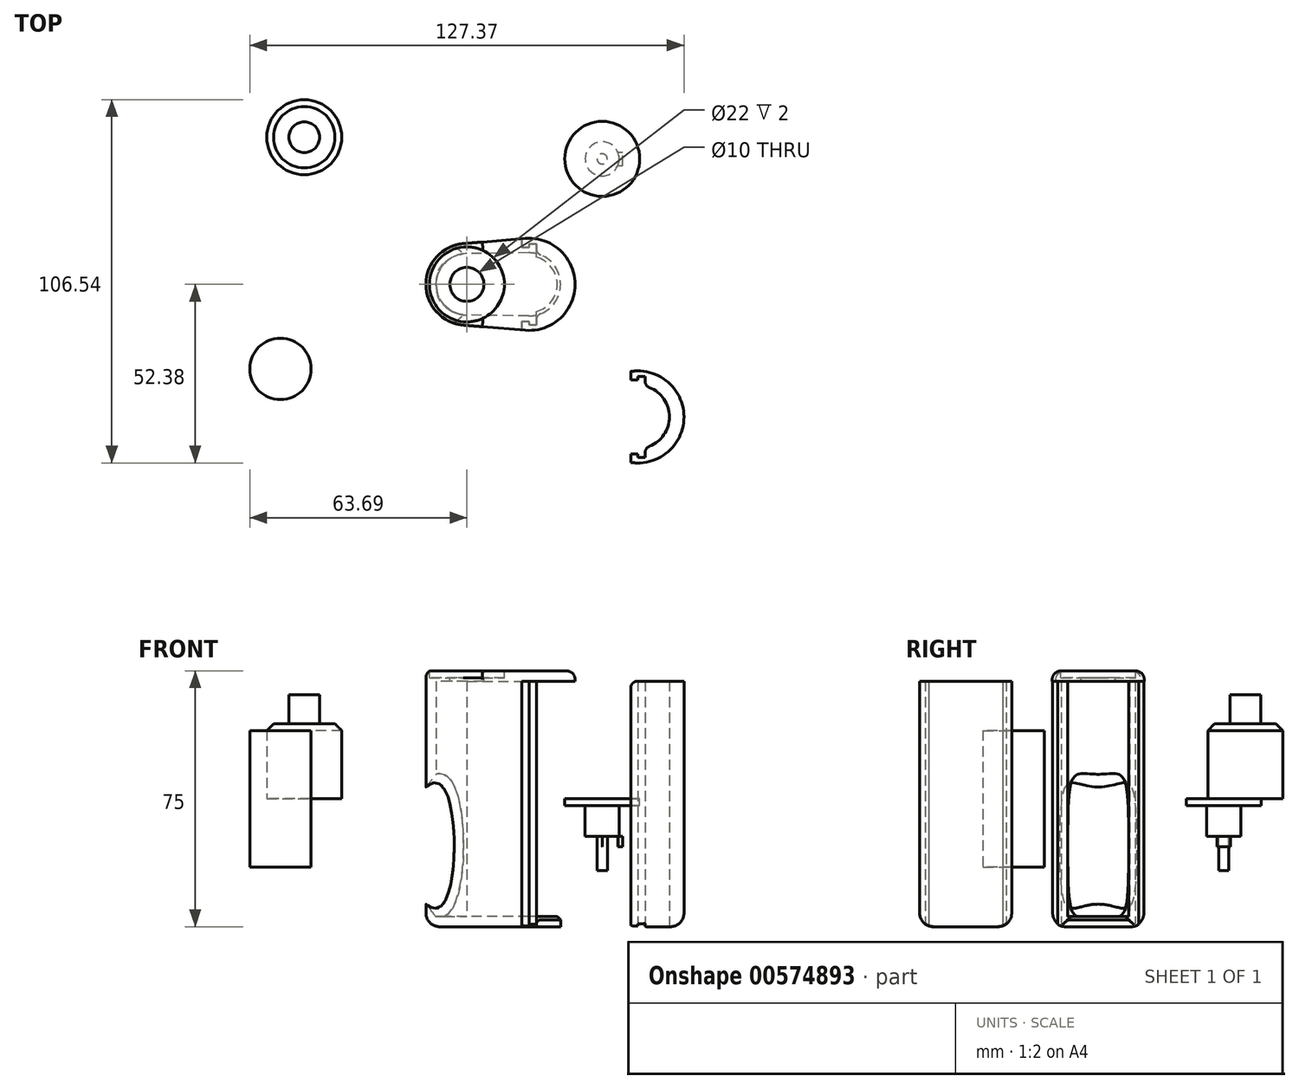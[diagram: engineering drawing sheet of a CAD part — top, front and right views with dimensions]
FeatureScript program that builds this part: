
annotation { "Feature Type Name" : "Feature", "Feature Type Description" : "" }
export const myFeature = defineFeature(function(context is Context, id is Id, definition is map)
    precondition{}
    {
        {
            var Q0;
            Q0=qCreatedBy(makeId("Top.planeOp"),FACE);
            var sketch = newSketch(context, id + "F0", { "sketchPlane" : qUnion([Q0])});
            skArc(sketch, "E0", {"start": v(20.38, 9) * mm, "mid": v(19.26, 9.2) * mm, "end": v(18.12, 9.25) * mm});
            skArc(sketch, "E1", {"start": v(-0.99, 11.96) * mm, "mid": v(-12, 0) * mm, "end": v(-0.99, -11.96) * mm});
            skArc(sketch, "E2", {"start": v(17.14, -13.45) * mm, "mid": v(31.75, 0) * mm, "end": v(17.14, 13.45) * mm});
            skLineSegment(sketch, "E3", {"start": v(17.14, 13.45) * mm, "end": v(-0.99, 11.96) * mm});
            skLineSegment(sketch, "E4", {"start": v(-0.99, -11.96) * mm, "end": v(17.14, -13.45) * mm});
            skPoint(sketch, "E5", {"position": v(18.25, 11.38) * mm});
            skPoint(sketch, "E6", {"position": v(18.25, -11.38) * mm});
            skLineSegment(sketch, "E7", {"start": v(18.25, 11.38) * mm, "end": v(18.25, 11.9) * mm});
            skLineSegment(sketch, "E8", {"start": v(18.25, 11.38) * mm, "end": v(18.25, 10.85) * mm});
            skLineSegment(sketch, "E9", {"start": v(18.25, -11.38) * mm, "end": v(18.25, -10.85) * mm});
            skLineSegment(sketch, "E10", {"start": v(18.25, -11.38) * mm, "end": v(18.25, -11.9) * mm});
            skLineSegment(sketch, "E11", {"start": v(18.25, -11.9) * mm, "end": v(20.38, -11.9) * mm});
            skLineSegment(sketch, "E12", {"start": v(18.25, -10.85) * mm, "end": v(16.12, -10.85) * mm});
            skLineSegment(sketch, "E13", {"start": v(18.25, 10.85) * mm, "end": v(16.13, 10.85) * mm});
            skLineSegment(sketch, "E14", {"start": v(18.25, 11.9) * mm, "end": v(20.38, 11.9) * mm});
            skLineSegment(sketch, "E15", {"start": v(16.13, 10.85) * mm, "end": v(16.13, 13.37) * mm});
            skLineSegment(sketch, "E16", {"start": v(20.38, 11.9) * mm, "end": v(20.38, 9) * mm});
            skLineSegment(sketch, "E17", {"start": v(16.12, -10.85) * mm, "end": v(16.12, -13.37) * mm});
            skLineSegment(sketch, "E18", {"start": v(20.38, -11.9) * mm, "end": v(20.38, -9) * mm});
            skPoint(sketch, "E19.orphan", {"position": v(16.13, 11.38) * mm});
            skPoint(sketch, "E20.end.orphan", {"position": v(20.38, 11.38) * mm});
            skPoint(sketch, "E21.orphan", {"position": v(16.12, -11.38) * mm});
            skPoint(sketch, "E22.end.orphan", {"position": v(20.38, -11.38) * mm});
            skArc(sketch, "E23", {"start": v(0, 9) * mm, "mid": v(-9, 0) * mm, "end": v(0, -9) * mm});
            skLineSegment(sketch, "E24", {"start": v(0, 9) * mm, "end": v(18.12, 9.25) * mm});
            skLineSegment(sketch, "E25", {"start": v(0, -9) * mm, "end": v(18.12, -9.25) * mm});
            skArc(sketch, "E26.trimOffspring", {"start": v(18.12, -9.25) * mm, "mid": v(19.26, -9.2) * mm, "end": v(20.37, -9) * mm});
            skSolve(sketch);
        }
        {
            var Q0;
            Q0=makeQuery(id+"F0.imprint","IMPRINT",FACE,{"disambiguationData":[TD([[makeQuery(id+"F0.imprint","IMPRINT",EDGE,{"derivedFrom":sQuery(id+"F0.wireOp",EDGE,"E0")}),-1.0]])]});
            extrude(context, id + "F1", {"entities" : qUnion([Q0]), "endBound" : BoundingType.SYMMETRIC, "depth" : 75 * mm, "offsetDistance" : 25 * mm});
        }
        {
            var Q0;
            Q0=makeQuery(id+"F1.opExtrude","CAP_FACE",FACE,{"disambiguationData":[OSD([sQuery(id+"F0.wireOp",EDGE,"E0"),sQuery(id+"F0.wireOp",EDGE,"E1"),sQuery(id+"F0.wireOp",EDGE,"E3"),sQuery(id+"F0.wireOp",EDGE,"E4"),sQuery(id+"F0.wireOp",EDGE,"E7"),sQuery(id+"F0.wireOp",EDGE,"E8"),sQuery(id+"F0.wireOp",EDGE,"E9"),sQuery(id+"F0.wireOp",EDGE,"E10"),sQuery(id+"F0.wireOp",EDGE,"E11"),sQuery(id+"F0.wireOp",EDGE,"E12"),sQuery(id+"F0.wireOp",EDGE,"E13"),sQuery(id+"F0.wireOp",EDGE,"E14"),sQuery(id+"F0.wireOp",EDGE,"E15"),sQuery(id+"F0.wireOp",EDGE,"E16"),sQuery(id+"F0.wireOp",EDGE,"E17"),sQuery(id+"F0.wireOp",EDGE,"E18"),sQuery(id+"F0.wireOp",EDGE,"E23"),sQuery(id+"F0.wireOp",EDGE,"E24"),sQuery(id+"F0.wireOp",EDGE,"E25"),sQuery(id+"F0.wireOp",EDGE,"E26.trimOffspring")])],"isStart":false});
            var sketch = newSketch(context, id + "F2", { "sketchPlane" : qUnion([Q0])});
            skArc(sketch, "E27", {"start": v(-0.99, 11.96) * mm, "mid": v(-12, 0) * mm, "end": v(-0.99, -11.96) * mm});
            skArc(sketch, "E28", {"start": v(17.14, -13.45) * mm, "mid": v(31.75, 0) * mm, "end": v(17.14, 13.45) * mm});
            skLineSegment(sketch, "E29", {"start": v(17.14, 13.45) * mm, "end": v(-0.99, 11.96) * mm});
            skLineSegment(sketch, "E30", {"start": v(-0.99, -11.96) * mm, "end": v(17.14, -13.45) * mm});
            skPoint(sketch, "E31", {"position": v(18.25, 11.38) * mm});
            skPoint(sketch, "E32", {"position": v(18.25, -11.38) * mm});
            skPoint(sketch, "E33.orphan", {"position": v(16.12, 11.38) * mm});
            skPoint(sketch, "E34.end.orphan", {"position": v(20.38, 11.38) * mm});
            skPoint(sketch, "E35.orphan", {"position": v(16.12, -11.38) * mm});
            skPoint(sketch, "E36.end.orphan", {"position": v(20.38, -11.38) * mm});
            skPoint(sketch, "E37.start.orphan", {"position": v(16.12, 10.85) * mm});
            skPoint(sketch, "E38.orphan", {"position": v(20.38, 11.9) * mm});
            skPoint(sketch, "E39.start.orphan", {"position": v(18.25, -11.9) * mm});
            skPoint(sketch, "E40.start.orphan", {"position": v(20.38, -11.9) * mm});
            skPoint(sketch, "E41.orphan", {"position": v(16.12, -10.85) * mm});
            skSolve(sketch);
        }
        {
            var Q0;
            {var subQ0=sQuery(id+"F2.wireOp",EDGE,"E28");Q0=makeQuery(id+"F2.imprint","IMPRINT",FACE,{"disambiguationData":[TD([[makeQuery(id+"F2.imprint","IMPRINT",EDGE,{"derivedFrom":subQ0}),1.0]])]});}
            var Q1;
            Q1 = qSketchRegion(id + "F4", true);
            extrude(context, id + "F3", {"entities" : qUnion([Q0, Q1]), "operationType" : NewBodyOperationType.ADD, "oppositeDirection" : true, "depth" : 3 * mm, "offsetDistance" : 25 * mm});
        }
        {
            var Q0;
            Q0=makeQuery(id+"F1.opExtrude","CAP_FACE",FACE,{"disambiguationData":[OSD([sQuery(id+"F0.wireOp",EDGE,"E0"),sQuery(id+"F0.wireOp",EDGE,"E1"),sQuery(id+"F0.wireOp",EDGE,"E3"),sQuery(id+"F0.wireOp",EDGE,"E4"),sQuery(id+"F0.wireOp",EDGE,"E7"),sQuery(id+"F0.wireOp",EDGE,"E8"),sQuery(id+"F0.wireOp",EDGE,"E9"),sQuery(id+"F0.wireOp",EDGE,"E10"),sQuery(id+"F0.wireOp",EDGE,"E11"),sQuery(id+"F0.wireOp",EDGE,"E12"),sQuery(id+"F0.wireOp",EDGE,"E13"),sQuery(id+"F0.wireOp",EDGE,"E14"),sQuery(id+"F0.wireOp",EDGE,"E15"),sQuery(id+"F0.wireOp",EDGE,"E16"),sQuery(id+"F0.wireOp",EDGE,"E17"),sQuery(id+"F0.wireOp",EDGE,"E18"),sQuery(id+"F0.wireOp",EDGE,"E23"),sQuery(id+"F0.wireOp",EDGE,"E24"),sQuery(id+"F0.wireOp",EDGE,"E25"),sQuery(id+"F0.wireOp",EDGE,"E26.trimOffspring")])],"isStart":true});
            var sketch = newSketch(context, id + "F4", { "sketchPlane" : qUnion([Q0])});
            skArc(sketch, "E42", {"start": v(-0.99, 11.96) * mm, "mid": v(-12, 0) * mm, "end": v(-0.99, -11.96) * mm});
            skLineSegment(sketch, "E43", {"start": v(16.12, 13.37) * mm, "end": v(-0.99, 11.96) * mm});
            skLineSegment(sketch, "E44", {"start": v(-0.99, -11.96) * mm, "end": v(16.13, -13.37) * mm});
            skPoint(sketch, "E45", {"position": v(18.25, 11.38) * mm});
            skPoint(sketch, "E46", {"position": v(18.25, -11.38) * mm});
            skLineSegment(sketch, "E47", {"start": v(18.25, 11.38) * mm, "end": v(18.25, 11.9) * mm});
            skLineSegment(sketch, "E48", {"start": v(18.25, 11.38) * mm, "end": v(18.25, 10.85) * mm});
            skLineSegment(sketch, "E49", {"start": v(18.25, -11.38) * mm, "end": v(18.25, -10.85) * mm});
            skLineSegment(sketch, "E50", {"start": v(18.25, -11.38) * mm, "end": v(18.25, -11.9) * mm});
            skLineSegment(sketch, "E51", {"start": v(18.25, -11.9) * mm, "end": v(20.38, -11.9) * mm});
            skLineSegment(sketch, "E52", {"start": v(18.25, -10.85) * mm, "end": v(16.12, -10.85) * mm});
            skLineSegment(sketch, "E53", {"start": v(18.25, 10.85) * mm, "end": v(16.12, 10.85) * mm});
            skLineSegment(sketch, "E54", {"start": v(18.25, 11.9) * mm, "end": v(20.38, 11.9) * mm});
            skLineSegment(sketch, "E55", {"start": v(16.12, 10.85) * mm, "end": v(16.12, 13.37) * mm});
            skLineSegment(sketch, "E56", {"start": v(20.38, 11.9) * mm, "end": v(20.38, 9) * mm});
            skLineSegment(sketch, "E57", {"start": v(16.12, -10.85) * mm, "end": v(16.12, -13.37) * mm});
            skLineSegment(sketch, "E58", {"start": v(20.38, -11.9) * mm, "end": v(20.38, -9) * mm});
            skPoint(sketch, "E59.orphan", {"position": v(16.12, 11.38) * mm});
            skPoint(sketch, "E60.end.orphan", {"position": v(20.38, 11.38) * mm});
            skPoint(sketch, "E61.orphan", {"position": v(16.12, -11.38) * mm});
            skPoint(sketch, "E62.end.orphan", {"position": v(20.38, -11.38) * mm});
            skArc(sketch, "E63", {"start": v(20.38, -9) * mm, "mid": v(27.5, 0) * mm, "end": v(20.38, 9) * mm});
            skSolve(sketch);
        }
        {
            var Q0;
            Q0 = qSketchRegion(id + "F4", true);
            extrude(context, id + "F5", {"entities" : qUnion([Q0]), "operationType" : NewBodyOperationType.ADD, "oppositeDirection" : true, "depth" : 3 * mm, "offsetDistance" : 25 * mm});
        }
        {
            var Q0;
            {var subQ0=sQuery(id+"F0.wireOp",EDGE,"E26.trimOffspring");var subQ1=sQuery(id+"F0.wireOp",EDGE,"E25");var subQ2=sQuery(id+"F0.wireOp",EDGE,"E24");var subQ3=sQuery(id+"F0.wireOp",EDGE,"E23");var subQ4=sQuery(id+"F0.wireOp",EDGE,"E18");var subQ5=sQuery(id+"F0.wireOp",EDGE,"E17");var subQ6=sQuery(id+"F0.wireOp",EDGE,"E16");var subQ7=sQuery(id+"F0.wireOp",EDGE,"E15");var subQ8=sQuery(id+"F0.wireOp",EDGE,"E14");var subQ9=sQuery(id+"F0.wireOp",EDGE,"E13");var subQ10=sQuery(id+"F0.wireOp",EDGE,"E12");var subQ11=sQuery(id+"F0.wireOp",EDGE,"E11");var subQ12=sQuery(id+"F0.wireOp",EDGE,"E10");var subQ13=sQuery(id+"F0.wireOp",EDGE,"E9");var subQ14=sQuery(id+"F0.wireOp",EDGE,"E8");var subQ15=sQuery(id+"F0.wireOp",EDGE,"E7");var subQ16=sQuery(id+"F0.wireOp",EDGE,"E0");Q0=makeQuery(id+"F3.boolean.opBoolean","MERGE",FACE,{"derivedFrom":[makeQuery(id+"F1.opExtrude","CAP_FACE",FACE,{"disambiguationData":[OSD([subQ16,sQuery(id+"F0.wireOp",EDGE,"E1"),sQuery(id+"F0.wireOp",EDGE,"E3"),sQuery(id+"F0.wireOp",EDGE,"E4"),subQ15,subQ14,subQ13,subQ12,subQ11,subQ10,subQ9,subQ8,subQ7,subQ6,subQ5,subQ4,subQ3,subQ2,subQ1,subQ0])],"isStart":false}),makeQuery(id+"F3.opExtrude","CAP_FACE",FACE,{"disambiguationData":[OSD([subQ16,subQ15,subQ14,subQ13,subQ12,subQ11,subQ10,subQ9,subQ8,subQ7,subQ6,subQ5,subQ4,subQ3,subQ2,subQ1,subQ0,sQuery(id+"F2.wireOp",EDGE,"E28"),sQuery(id+"F2.wireOp",EDGE,"E29"),sQuery(id+"F2.wireOp",EDGE,"E30")])],"isStart":true})]});}
            var sketch = newSketch(context, id + "F6", { "sketchPlane" : qUnion([Q0])});
            skCircle(sketch, "E64", {"center": v(0, 0) * mm, "radius": 11 * mm});
            skSolve(sketch);
        }
        {
            var Q0;
            Q0=makeQuery(id+"F6.imprint","IMPRINT",FACE,{"disambiguationData":[TD([[makeQuery(id+"F6.imprint","IMPRINT",EDGE,{"derivedFrom":sQuery(id+"F6.wireOp",EDGE,"E64")}),1.0]])]});
            extrude(context, id + "F7", {"entities" : qUnion([Q0]), "operationType" : NewBodyOperationType.REMOVE, "oppositeDirection" : true, "depth" : 2 * mm, "offsetDistance" : 25 * mm});
        }
        {
            var Q0;
            Q0=makeQuery(id+"F7.boolean.opBoolean","COPY",FACE,{"derivedFrom":makeQuery(id+"F7.opExtrude","CAP_FACE",FACE,{"disambiguationData":[OSD([sQuery(id+"F6.wireOp",EDGE,"E64")])],"isStart":false})});
            var sketch = newSketch(context, id + "F8", { "sketchPlane" : qUnion([Q0])});
            skCircle(sketch, "E65", {"center": v(0, 0) * mm, "radius": 5 * mm});
            skSolve(sketch);
        }
        {
            var Q0;
            Q0=makeQuery(id+"F8.imprint","IMPRINT",FACE,{"disambiguationData":[TD([[makeQuery(id+"F8.imprint","IMPRINT",EDGE,{"derivedFrom":sQuery(id+"F8.wireOp",EDGE,"E65")}),1.0]])]});
            var Q1;
            Q1=sQuery(id+"F8.wireOp",EDGE,"E65");
            extrude(context, id + "F9", {"entities" : qUnion([Q0]), "operationType" : NewBodyOperationType.REMOVE, "surfaceEntities" : qUnion([Q1]), "oppositeDirection" : true, "depth" : 13.8 * mm, "offsetDistance" : 25 * mm});
        }
        {
            var Q0;
            Q0=qCreatedBy(makeId("Top.planeOp"),FACE);
            var sketch = newSketch(context, id + "F10", { "sketchPlane" : qUnion([Q0])});
            skArc(sketch, "E66", {"start": v(52.3, -47.88) * mm, "mid": v(59.43, -38.88) * mm, "end": v(52.3, -29.88) * mm});
            skArc(sketch, "E67", {"start": v(49.08, -52.33) * mm, "mid": v(63.68, -38.88) * mm, "end": v(49.08, -25.43) * mm});
            skLineSegment(sketch, "E68", {"start": v(49.08, -25.43) * mm, "end": v(48.06, -25.5) * mm});
            skLineSegment(sketch, "E69", {"start": v(48.06, -52.25) * mm, "end": v(49.08, -52.33) * mm});
            skPoint(sketch, "E70", {"position": v(50.18, -27.5) * mm});
            skPoint(sketch, "E71", {"position": v(50.18, -50.26) * mm});
            skLineSegment(sketch, "E72", {"start": v(50.18, -27.5) * mm, "end": v(50.18, -26.98) * mm});
            skLineSegment(sketch, "E73", {"start": v(50.18, -27.5) * mm, "end": v(50.18, -28.04) * mm});
            skLineSegment(sketch, "E74", {"start": v(50.18, -50.26) * mm, "end": v(50.18, -49.73) * mm});
            skLineSegment(sketch, "E75", {"start": v(50.18, -50.26) * mm, "end": v(50.18, -50.79) * mm});
            skLineSegment(sketch, "E76", {"start": v(50.18, -50.79) * mm, "end": v(52.3, -50.79) * mm});
            skLineSegment(sketch, "E77", {"start": v(50.18, -49.73) * mm, "end": v(48.06, -49.73) * mm});
            skLineSegment(sketch, "E78", {"start": v(50.18, -28.04) * mm, "end": v(48.06, -28.04) * mm});
            skLineSegment(sketch, "E79", {"start": v(50.18, -26.98) * mm, "end": v(52.3, -26.98) * mm});
            skLineSegment(sketch, "E80", {"start": v(48.06, -28.04) * mm, "end": v(48.06, -25.5) * mm});
            skLineSegment(sketch, "E81", {"start": v(52.3, -26.98) * mm, "end": v(52.3, -29.88) * mm});
            skLineSegment(sketch, "E82", {"start": v(48.06, -49.73) * mm, "end": v(48.06, -52.25) * mm});
            skLineSegment(sketch, "E83", {"start": v(52.3, -50.79) * mm, "end": v(52.3, -47.88) * mm});
            skPoint(sketch, "E84.orphan", {"position": v(52.3, -27.5) * mm});
            skPoint(sketch, "E85.start.orphan", {"position": v(48.06, -27.5) * mm});
            skPoint(sketch, "E86.orphan", {"position": v(52.3, -50.26) * mm});
            skPoint(sketch, "E87.start.orphan", {"position": v(48.06, -50.26) * mm});
            skSolve(sketch);
        }
        {
            var Q0;
            Q0=makeQuery(id+"F10.imprint","IMPRINT",FACE,{"disambiguationData":[TD([[makeQuery(id+"F10.imprint","IMPRINT",EDGE,{"derivedFrom":sQuery(id+"F10.wireOp",EDGE,"E66")}),-1.0]])]});
            extrude(context, id + "F11", {"entities" : qUnion([Q0]), "depth" : 34.5 * mm, "offsetDistance" : 25 * mm, "hasSecondDirection" : true, "secondDirectionOppositeDirection" : true, "secondDirectionDepth" : 37.5 * mm});
        }
        {
            var Q0;
            Q0=qCreatedBy(makeId("Top.planeOp"),FACE);
            var sketch = newSketch(context, id + "F12", { "sketchPlane" : qUnion([Q0])});
            skCircle(sketch, "E88", {"center": v(-47.7, 43.16) * mm, "radius": 11 * mm});
            skSolve(sketch);
        }
        {
            var Q0;
            Q0=makeQuery(id+"F12.imprint","IMPRINT",FACE,{"disambiguationData":[TD([[makeQuery(id+"F12.imprint","IMPRINT",EDGE,{"derivedFrom":sQuery(id+"F12.wireOp",EDGE,"E88")}),1.0]])]});
            extrude(context, id + "F13", {"entities" : qUnion([Q0]), "depth" : 22 * mm, "offsetDistance" : 25 * mm});
        }
        {
            var Q0;
            Q0=makeQuery(id+"F13.opExtrude","CAP_FACE",FACE,{"disambiguationData":[OSD([sQuery(id+"F12.wireOp",EDGE,"E88")])],"isStart":false});
            var sketch = newSketch(context, id + "F14", { "sketchPlane" : qUnion([Q0])});
            skCircle(sketch, "E89", {"center": v(-47.7, 43.16) * mm, "radius": 4.5 * mm});
            skSolve(sketch);
        }
        {
            var Q0;
            Q0=makeQuery(id+"F14.imprint","IMPRINT",FACE,{"disambiguationData":[TD([[makeQuery(id+"F14.imprint","IMPRINT",EDGE,{"derivedFrom":sQuery(id+"F14.wireOp",EDGE,"E89")}),1.0]])]});
            extrude(context, id + "F15", {"entities" : qUnion([Q0]), "operationType" : NewBodyOperationType.ADD, "depth" : 8.5 * mm, "offsetDistance" : 25 * mm});
        }
        {
            var Q0;
            Q0=makeQuery(id+"F13.opExtrude","CAP_EDGE",EDGE,{"disambiguationData":[OSD([sQuery(id+"F12.wireOp",EDGE,"E88")])],"isStart":false});
            chamfer(context, id + "F16", {"entities" : qUnion([Q0]), "width" : 2 * mm, "tangentPropagation" : true});
        }
        {
            var Q0;
            Q0=qCreatedBy(makeId("Front.planeOp"),FACE);
            var sketch = newSketch(context, id + "F17", { "sketchPlane" : qUnion([Q0])});
            skEllipse(sketch, "E90", {"center": v(-13.2, -13.71) * mm, "majorRadius": 15.12 * mm, "minorRadius": 5.56 * mm, "majorAxis": v(0, -1)});
            skSolve(sketch);
        }
        {
            var Q0;
            Q0 = qSketchRegion(id + "F17", true);
            var Q1;
            Q1=makeQuery(id+"F17.imprint","IMPRINT",FACE,{"disambiguationData":[TD([[makeQuery(id+"F17.imprint","IMPRINT",EDGE,{"derivedFrom":sQuery(id+"F17.wireOp",EDGE,"E90")}),1.0]])]});
            extrude(context, id + "F18", {"entities" : qUnion([Q0, Q1]), "operationType" : NewBodyOperationType.REMOVE, "endBound" : BoundingType.SYMMETRIC, "oppositeDirection" : true, "depth" : 25 * mm, "offsetDistance" : 25 * mm});
        }
        {
            var Q0;
            Q0=makeQuery(id+"F18.boolean.opBoolean","INTERSECT",EDGE,{"derivedFrom":[makeQuery(id+"F1.opExtrude","SWEPT_FACE",FACE,{"disambiguationData":[OSD([sQuery(id+"F0.wireOp",EDGE,"E23")])]}),makeQuery(id+"F18.opExtrude","SWEPT_FACE",FACE,{"disambiguationData":[OSD([sQuery(id+"F17.wireOp",EDGE,"E90")])]})]});
            chamfer(context, id + "F19", {"entities" : qUnion([Q0]), "width" : 6 * mm, "tangentPropagation" : true});
        }
        {
            var Q0;
            Q0=qCreatedBy(makeId("Top.planeOp"),FACE);
            var sketch = newSketch(context, id + "F20", { "sketchPlane" : qUnion([Q0])});
            skCircle(sketch, "E91", {"center": v(-54.69, -24.8) * mm, "radius": 9 * mm});
            skSolve(sketch);
        }
        {
            var Q0;
            Q0=makeQuery(id+"F20.imprint","IMPRINT",FACE,{"disambiguationData":[TD([[makeQuery(id+"F20.imprint","IMPRINT",EDGE,{"derivedFrom":sQuery(id+"F20.wireOp",EDGE,"E91")}),1.0]])]});
            extrude(context, id + "F21", {"entities" : qUnion([Q0]), "endBound" : BoundingType.SYMMETRIC, "depth" : 40 * mm, "offsetDistance" : 25 * mm});
        }
        {
            var Q0;
            Q0=makeQuery(id+"F1.opExtrude","CAP_EDGE",EDGE,{"disambiguationData":[OSD([sQuery(id+"F0.wireOp",EDGE,"E1")])],"isStart":true});
            var Q1;
            Q1=makeQuery(id+"F11.opExtrude","CAP_EDGE",EDGE,{"disambiguationData":[OSD([sQuery(id+"F10.wireOp",EDGE,"E67")])],"isStart":true});
            var Q2;
            Q2=makeQuery(id+"F18.boolean.opBoolean","INTERSECT",EDGE,{"derivedFrom":[makeQuery(id+"F1.opExtrude","SWEPT_FACE",FACE,{"disambiguationData":[OSD([sQuery(id+"F0.wireOp",EDGE,"E1")])]}),makeQuery(id+"F18.opExtrude","SWEPT_FACE",FACE,{"disambiguationData":[OSD([sQuery(id+"F17.wireOp",EDGE,"E90")])]})]});
            fillet(context, id + "F22", {"entities" : qUnion([Q0, Q1, Q2]), "radius" : 4 * mm, "tangentPropagation" : true, "allowEdgeOverflow" : false});
        }
        {
            var Q0;
            Q0=makeQuery(id+"F3.opExtrude","CAP_EDGE",EDGE,{"disambiguationData":[OSD([sQuery(id+"F2.wireOp",EDGE,"E28")])],"isStart":true});
            fillet(context, id + "F23", {"entities" : qUnion([Q0]), "radius" : 2.5 * mm, "tangentPropagation" : true, "allowEdgeOverflow" : false});
        }
        {
            var Q0;
            Q0=makeQuery(id+"F3.opExtrude","CAP_EDGE",EDGE,{"disambiguationData":[OSD([sQuery(id+"F0.wireOp",EDGE,"E17")])],"isStart":false});
            var Q1;
            Q1=makeQuery(id+"F3.opExtrude","CAP_EDGE",EDGE,{"disambiguationData":[OSD([sQuery(id+"F0.wireOp",EDGE,"E15")])],"isStart":false});
            var Q2;
            Q2=makeQuery(id+"F11.opExtrude","CAP_EDGE",EDGE,{"disambiguationData":[OSD([sQuery(id+"F10.wireOp",EDGE,"E80")])],"isStart":false});
            var Q3;
            Q3=makeQuery(id+"F11.opExtrude","CAP_EDGE",EDGE,{"disambiguationData":[OSD([sQuery(id+"F10.wireOp",EDGE,"E82")])],"isStart":false});
            fillet(context, id + "F24", {"entities" : qUnion([Q0, Q1, Q2, Q3]), "radius" : 2 * mm, "tangentPropagation" : true, "allowEdgeOverflow" : false});
        }
        {
            var Q0;
            Q0=makeQuery(id+"F5.opExtrude","CAP_EDGE",EDGE,{"disambiguationData":[OSD([sQuery(id+"F4.wireOp",EDGE,"E63")])],"isStart":false});
            chamfer(context, id + "F25", {"entities" : qUnion([Q0]), "width" : 1 * mm, "tangentPropagation" : true});
        }
        {
            var Q0;
            Q0=makeQuery(id+"F11.opExtrude","SWEPT_EDGE",EDGE,{"disambiguationData":[OSD([sQuery(id+"F10.wireOp",EDGE,"E66"),sQuery(id+"F10.wireOp",EDGE,"E81")])]});
            var Q1;
            Q1=makeQuery(id+"F11.opExtrude","SWEPT_EDGE",EDGE,{"disambiguationData":[OSD([sQuery(id+"F10.wireOp",EDGE,"E66"),sQuery(id+"F10.wireOp",EDGE,"E83")])]});
            fillet(context, id + "F26", {"entities" : qUnion([Q0, Q1]), "radius" : 2 * mm, "tangentPropagation" : true, "allowEdgeOverflow" : false});
        }
        {
            var Q0;
            {var subQ0=sQuery(id+"F0.wireOp",EDGE,"E26.trimOffspring");Q0=makeQuery(id+"F5.boolean.opBoolean","MERGE",EDGE,{"derivedFrom":[makeQuery(id+"F1.opExtrude","SWEPT_EDGE",EDGE,{"disambiguationData":[OSD([sQuery(id+"F0.wireOp",EDGE,"E18"),subQ0])]}),makeQuery(id+"F5.opExtrude","SWEPT_EDGE",EDGE,{"disambiguationData":[OSD([subQ0,sQuery(id+"F4.wireOp",EDGE,"E56"),sQuery(id+"F4.wireOp",EDGE,"E63")])]})]});}
            var Q1;
            {var subQ0=sQuery(id+"F0.wireOp",EDGE,"E0");Q1=makeQuery(id+"F5.boolean.opBoolean","MERGE",EDGE,{"derivedFrom":[makeQuery(id+"F1.opExtrude","SWEPT_EDGE",EDGE,{"disambiguationData":[OSD([subQ0,sQuery(id+"F0.wireOp",EDGE,"E16")])]}),makeQuery(id+"F5.opExtrude","SWEPT_EDGE",EDGE,{"disambiguationData":[OSD([subQ0,sQuery(id+"F4.wireOp",EDGE,"E58"),sQuery(id+"F4.wireOp",EDGE,"E63")])]})]});}
            fillet(context, id + "F27", {"entities" : qUnion([Q0, Q1]), "radius" : 2 * mm, "tangentPropagation" : true, "allowEdgeOverflow" : false});
        }
        {
            var Q0;
            Q0=qCreatedBy(makeId("Top.planeOp"),FACE);
            var sketch = newSketch(context, id + "F28", { "sketchPlane" : qUnion([Q0])});
            skCircle(sketch, "E92", {"center": v(39.7, 36.8) * mm, "radius": 11 * mm});
            skSolve(sketch);
        }
        {
            var Q0;
            Q0=makeQuery(id+"F28.imprint","IMPRINT",FACE,{"disambiguationData":[TD([[makeQuery(id+"F28.imprint","IMPRINT",EDGE,{"derivedFrom":sQuery(id+"F28.wireOp",EDGE,"E92")}),1.0]])]});
            extrude(context, id + "F29", {"entities" : qUnion([Q0]), "oppositeDirection" : true, "depth" : 2 * mm, "offsetDistance" : 25 * mm});
        }
        {
            var Q0;
            Q0=makeQuery(id+"F29.opExtrude","CAP_FACE",FACE,{"disambiguationData":[OSD([sQuery(id+"F28.wireOp",EDGE,"E92")])],"isStart":false});
            var sketch = newSketch(context, id + "F30", { "sketchPlane" : qUnion([Q0])});
            skCircle(sketch, "E93", {"center": v(39.7, -36.8) * mm, "radius": 5 * mm});
            skSolve(sketch);
        }
        {
            var Q0;
            Q0=makeQuery(id+"F30.imprint","IMPRINT",FACE,{"disambiguationData":[TD([[makeQuery(id+"F30.imprint","IMPRINT",EDGE,{"derivedFrom":sQuery(id+"F30.wireOp",EDGE,"E93")}),1.0]])]});
            extrude(context, id + "F31", {"entities" : qUnion([Q0]), "operationType" : NewBodyOperationType.ADD, "depth" : 9 * mm, "offsetDistance" : 25 * mm});
        }
        {
            var Q0;
            Q0=makeQuery(id+"F31.opExtrude","CAP_FACE",FACE,{"disambiguationData":[OSD([sQuery(id+"F30.wireOp",EDGE,"E93")])],"isStart":false});
            var sketch = newSketch(context, id + "F32", { "sketchPlane" : qUnion([Q0])});
            skCircle(sketch, "E94", {"center": v(39.7, -36.8) * mm, "radius": 1.5 * mm});
            skSolve(sketch);
        }
        {
            var Q0;
            Q0=makeQuery(id+"F32.imprint","IMPRINT",FACE,{"disambiguationData":[TD([[makeQuery(id+"F32.imprint","IMPRINT",EDGE,{"derivedFrom":sQuery(id+"F32.wireOp",EDGE,"E94")}),1.0]])]});
            extrude(context, id + "F33", {"entities" : qUnion([Q0]), "operationType" : NewBodyOperationType.ADD, "depth" : 10 * mm, "offsetDistance" : 25 * mm});
        }
        {
            var Q0;
            Q0=makeQuery(id+"F31.opExtrude","CAP_FACE",FACE,{"disambiguationData":[OSD([sQuery(id+"F30.wireOp",EDGE,"E93")])],"isStart":false});
            var sketch = newSketch(context, id + "F34", { "sketchPlane" : qUnion([Q0])});
            skArc(sketch, "E95", {"start": v(39.72, -34.8) * mm, "mid": v(37.7, -36.8) * mm, "end": v(39.72, -38.8) * mm});
            skLineSegment(sketch, "E96", {"start": v(39.68, -34.8) * mm, "end": v(45.68, -34.8) * mm});
            skLineSegment(sketch, "E97", {"start": v(39.72, -38.8) * mm, "end": v(45.72, -38.8) * mm});
            skLineSegment(sketch, "E98", {"start": v(45.68, -34.8) * mm, "end": v(45.72, -38.8) * mm});
            skSolve(sketch);
        }
        {
            var Q0;
            {var subQ1=sQuery(id+"F34.wireOp",EDGE,"E95");Q0=makeQuery(id+"F34.imprint","IMPRINT",FACE,{"disambiguationData":[TD([[makeQuery(id+"F34.imprint","IMPRINT",EDGE,{"derivedFrom":subQ1}),1.0]])]});}
            var Q1;
            {var subQ0=sQuery(id+"F34.wireOp",EDGE,"E98");Q1=makeQuery(id+"F34.imprint","IMPRINT",FACE,{"disambiguationData":[TD([[makeQuery(id+"F34.imprint","IMPRINT",EDGE,{"derivedFrom":subQ0}),-1.0]])]});}
            extrude(context, id + "F35", {"entities" : qUnion([Q0, Q1]), "depth" : 3 * mm, "offsetDistance" : 50 * mm});
        }
    });
